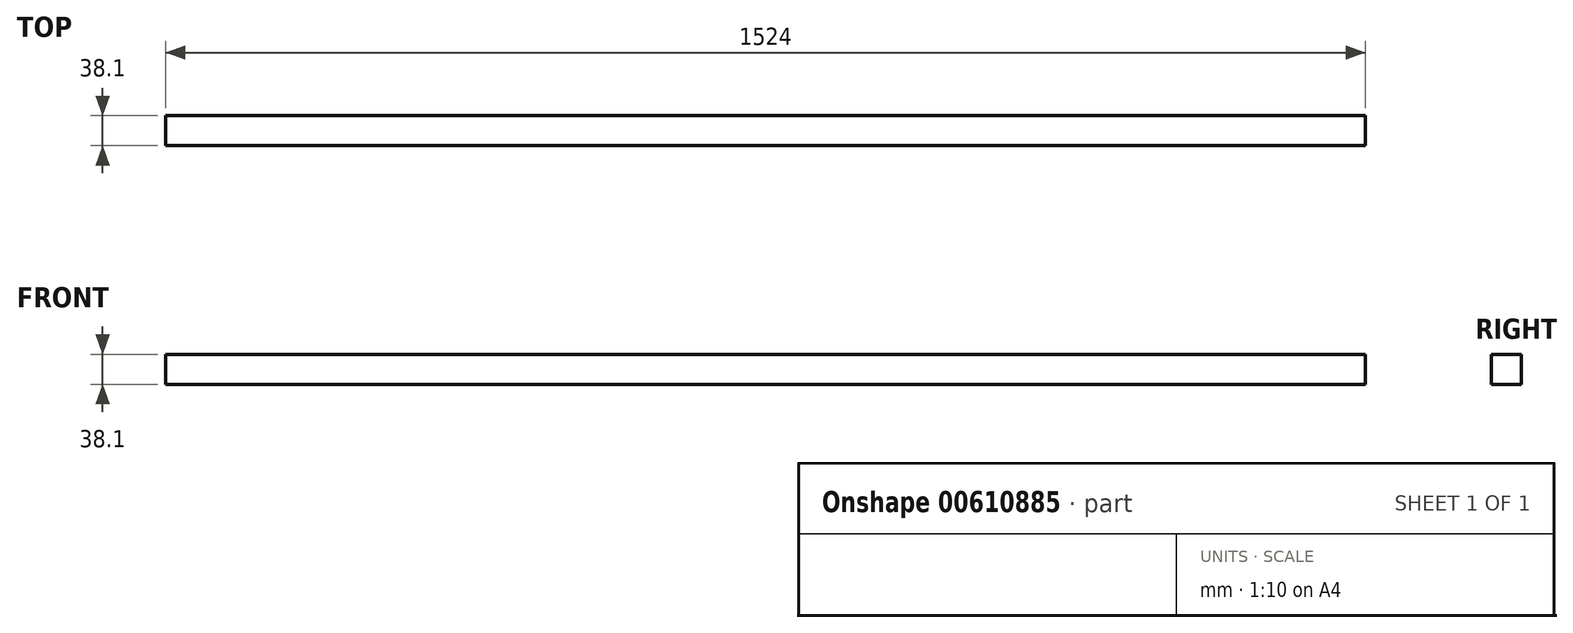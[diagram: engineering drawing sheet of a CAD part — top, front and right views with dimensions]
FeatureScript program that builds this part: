
annotation { "Feature Type Name" : "Feature", "Feature Type Description" : "" }
export const myFeature = defineFeature(function(context is Context, id is Id, definition is map)
    precondition{}
    {
        {
            var Q0;
            Q0=qCreatedBy(makeId("Top.planeOp"),FACE);
            var sketch = newSketch(context, id + "F0", { "sketchPlane" : qUnion([Q0])});
            skLineSegment(sketch, "E0.bottom", {"start": v(-762, 368.3) * mm, "end": v(762, 368.3) * mm});
            skLineSegment(sketch, "E0.top", {"start": v(-762, -368.3) * mm, "end": v(762, -368.3) * mm});
            skLineSegment(sketch, "E0.left", {"start": v(-762, 368.3) * mm, "end": v(-762, -368.3) * mm});
            skLineSegment(sketch, "E0.right", {"start": v(762, 368.3) * mm, "end": v(762, -368.3) * mm});
            skPoint(sketch, "E0.middle", {"position": v(0, 0) * mm});
            skPoint(sketch, "E1", {"position": v(762, -317.5) * mm});
            skLineSegment(sketch, "E2", {"start": v(762, -317.5) * mm, "end": v(-762, -317.5) * mm});
            skLineSegment(sketch, "E3.bottom", {"start": v(723.9, 330.2) * mm, "end": v(-723.9, 330.2) * mm});
            skLineSegment(sketch, "E3.top", {"start": v(723.9, -279.4) * mm, "end": v(-723.9, -279.4) * mm});
            skLineSegment(sketch, "E3.left", {"start": v(723.9, 330.2) * mm, "end": v(723.9, -279.4) * mm});
            skLineSegment(sketch, "E3.right", {"start": v(-723.9, 330.2) * mm, "end": v(-723.9, -279.4) * mm});
            skLineSegment(sketch, "E4", {"start": v(-723.9, -279.4) * mm, "end": v(-762, -279.4) * mm});
            skLineSegment(sketch, "E5", {"start": v(723.9, -279.4) * mm, "end": v(762, -279.4) * mm});
            skLineSegment(sketch, "E6", {"start": v(723.9, 330.2) * mm, "end": v(762, 330.2) * mm});
            skLineSegment(sketch, "E7", {"start": v(-723.9, 330.2) * mm, "end": v(-762, 330.2) * mm});
            skLineSegment(sketch, "E8.bottom", {"start": v(-723.9, 330.2) * mm, "end": v(-635, 330.2) * mm});
            skLineSegment(sketch, "E8.top", {"start": v(-723.9, 241.3) * mm, "end": v(-635, 241.3) * mm});
            skLineSegment(sketch, "E8.left", {"start": v(-723.9, 330.2) * mm, "end": v(-723.9, 241.3) * mm});
            skLineSegment(sketch, "E8.right", {"start": v(-635, 330.2) * mm, "end": v(-635, 241.3) * mm});
            skLineSegment(sketch, "E9.bottom", {"start": v(-723.9, -279.4) * mm, "end": v(-635, -279.4) * mm});
            skLineSegment(sketch, "E9.top", {"start": v(-723.9, -190.5) * mm, "end": v(-635, -190.5) * mm});
            skLineSegment(sketch, "E9.left", {"start": v(-723.9, -279.4) * mm, "end": v(-723.9, -190.5) * mm});
            skLineSegment(sketch, "E9.right", {"start": v(-635, -279.4) * mm, "end": v(-635, -190.5) * mm});
            skLineSegment(sketch, "E10.MirrorCS", {"start": v(723.9, 241.3) * mm, "end": v(635, 241.3) * mm});
            skLineSegment(sketch, "E11.MirrorCS", {"start": v(635, 330.2) * mm, "end": v(635, 241.3) * mm});
            skLineSegment(sketch, "E12.MirrorCS", {"start": v(723.9, -190.5) * mm, "end": v(635, -190.5) * mm});
            skLineSegment(sketch, "E13.MirrorCS", {"start": v(635, -279.4) * mm, "end": v(635, -190.5) * mm});
            skPoint(sketch, "E14", {"position": v(-723.9, 285.75) * mm});
            skPoint(sketch, "E15", {"position": v(-723.9, -234.95) * mm});
            skSolve(sketch);
        }
        {
            var Q0;
            Q0=makeQuery(id+"F0.imprint","IMPRINT",FACE,{"disambiguationData":[TD([[makeQuery(id+"F0.imprint","IMPRINT",EDGE,{"derivedFrom":sQuery(id+"F0.wireOp",EDGE,"E0.bottom")}),-1.0]])]});
            extrude(context, id + "F1", {"entities" : qUnion([Q0]), "depth" : 38.1 * mm, "offsetDistance" : 25.4 * mm});
        }
    });
